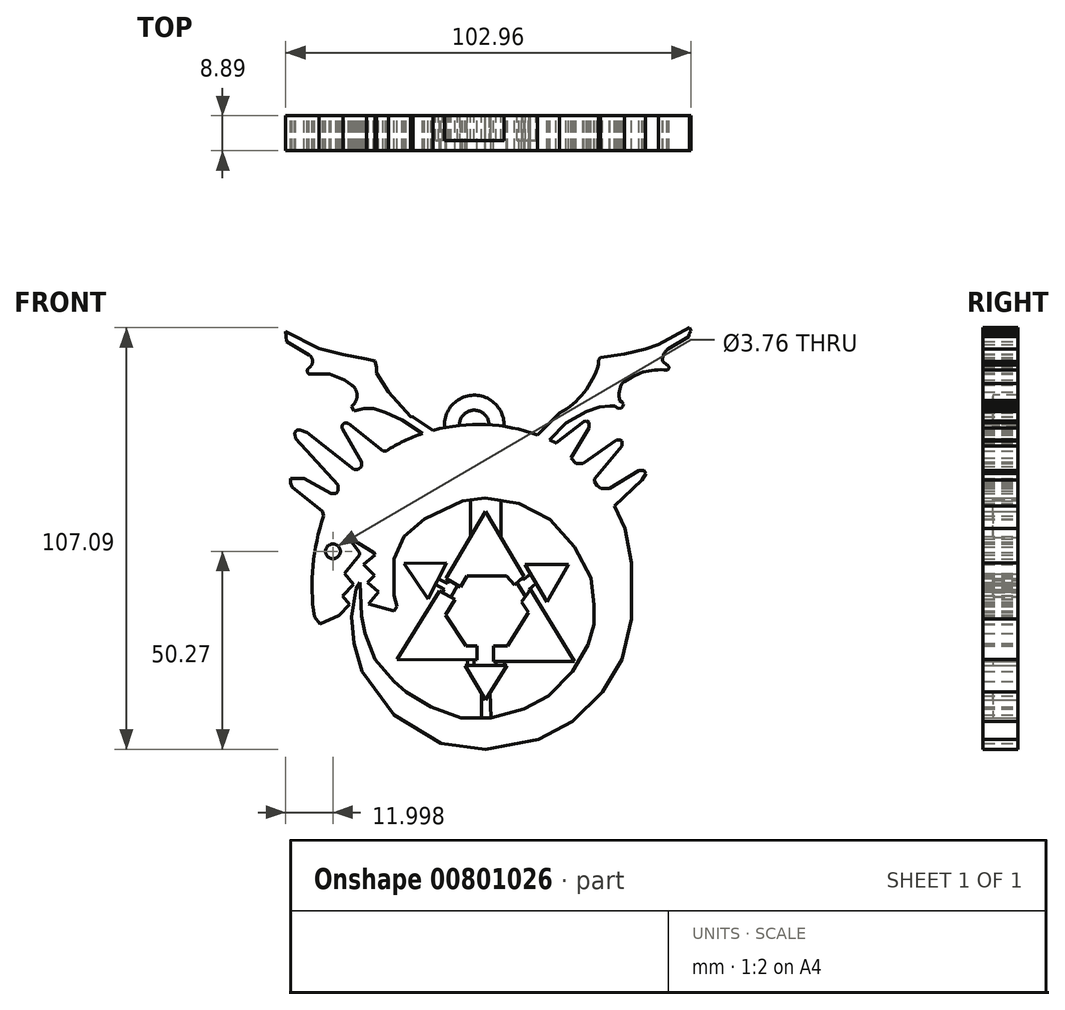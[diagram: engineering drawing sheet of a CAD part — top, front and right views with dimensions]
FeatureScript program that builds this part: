
annotation { "Feature Type Name" : "Feature", "Feature Type Description" : "" }
export const myFeature = defineFeature(function(context is Context, id is Id, definition is map)
    precondition{}
    {
        {
            var Q0;
            Q0=qCreatedBy(makeId("Front.planeOp"),FACE);
            var sketch = newSketch(context, id + "F0", { "sketchPlane" : qUnion([Q0])});
            skLineSegment(sketch, "E0", {"start": v(4.77, 15.18) * mm, "end": v(-5.28, -1.88) * mm});
            skLineSegment(sketch, "E1", {"start": v(-5.28, -1.88) * mm, "end": v(-1.66, -4) * mm});
            skLineSegment(sketch, "E2", {"start": v(-1.66, -4) * mm, "end": v(0, -1.18) * mm});
            skLineSegment(sketch, "E3", {"start": v(0, -1.18) * mm, "end": v(10.1, -1.18) * mm});
            skLineSegment(sketch, "E4", {"start": v(10.1, -1.18) * mm, "end": v(12.07, -3.5) * mm});
            skLineSegment(sketch, "E5", {"start": v(12.07, -3.5) * mm, "end": v(14.56, -1.36) * mm});
            skLineSegment(sketch, "E6", {"start": v(14.56, -1.36) * mm, "end": v(4.77, 15.18) * mm});
            skLineSegment(sketch, "E7", {"start": v(-15.93, 1.95) * mm, "end": v(-9.92, -7.03) * mm});
            skLineSegment(sketch, "E8", {"start": v(-9.92, -7.03) * mm, "end": v(-5.15, 2.13) * mm});
            skLineSegment(sketch, "E9", {"start": v(-5.15, 2.13) * mm, "end": v(-15.93, 1.95) * mm});
            skLineSegment(sketch, "E10", {"start": v(-6.9, -5.02) * mm, "end": v(-17.71, -22.44) * mm});
            skLineSegment(sketch, "E11", {"start": v(-17.71, -22.44) * mm, "end": v(2.58, -22.54) * mm});
            skLineSegment(sketch, "E12", {"start": v(-0.25, -18.9) * mm, "end": v(-5.46, -11.12) * mm});
            skLineSegment(sketch, "E13", {"start": v(-5.46, -11.12) * mm, "end": v(-2.97, -7.1) * mm});
            skLineSegment(sketch, "E14", {"start": v(-2.97, -7.1) * mm, "end": v(-6.9, -5.02) * mm});
            skLineSegment(sketch, "E15", {"start": v(13.84, -7.73) * mm, "end": v(15.64, -10.43) * mm});
            skLineSegment(sketch, "E16", {"start": v(15.64, -10.43) * mm, "end": v(10.38, -18.9) * mm});
            skLineSegment(sketch, "E17", {"start": v(10.38, -18.9) * mm, "end": v(6.72, -18.9) * mm});
            skLineSegment(sketch, "E18", {"start": v(6.72, -18.9) * mm, "end": v(6.72, -22.35) * mm});
            skLineSegment(sketch, "E19", {"start": v(6.72, -22.35) * mm, "end": v(6.72, -22.9) * mm});
            skLineSegment(sketch, "E20", {"start": v(6.72, -22.9) * mm, "end": v(27.35, -22.9) * mm});
            skLineSegment(sketch, "E21", {"start": v(27.35, -22.9) * mm, "end": v(16.18, -4.59) * mm});
            skLineSegment(sketch, "E22", {"start": v(16.18, -4.59) * mm, "end": v(13.84, -7.73) * mm});
            skLineSegment(sketch, "E23", {"start": v(14.74, 1.75) * mm, "end": v(25.78, 1.75) * mm});
            skPoint(sketch, "E23.startSnap0", {"position": v(14.74, -9.08) * mm});
            skLineSegment(sketch, "E24", {"start": v(25.78, 1.75) * mm, "end": v(20.37, -7.73) * mm});
            skLineSegment(sketch, "E25", {"start": v(20.37, -7.73) * mm, "end": v(14.74, 1.75) * mm});
            skLineSegment(sketch, "E26", {"start": v(4.77, -32.65) * mm, "end": v(10.23, -23.87) * mm});
            skLineSegment(sketch, "E27", {"start": v(10.23, -23.87) * mm, "end": v(-0.4, -23.87) * mm});
            skLineSegment(sketch, "E28", {"start": v(-0.4, -23.87) * mm, "end": v(4.77, -32.65) * mm});
            skCircle(sketch, "E29", {"center": v(-34.01, 5.06) * mm, "radius": 1.88 * mm});
            skLineSegment(sketch, "E30", {"start": v(-32.5, -11.2) * mm, "end": v(-29.8, -8.4) * mm});
            skLineSegment(sketch, "E31", {"start": v(-29.8, -8.4) * mm, "end": v(-31.63, -6.25) * mm});
            skLineSegment(sketch, "E32", {"start": v(-31.63, -6.25) * mm, "end": v(-28.79, -3.38) * mm});
            skLineSegment(sketch, "E33", {"start": v(-28.79, -3.38) * mm, "end": v(-31.12, -0.5) * mm});
            skLineSegment(sketch, "E34", {"start": v(-31.12, -0.5) * mm, "end": v(-27.2, 4.16) * mm});
            skLineSegment(sketch, "E35", {"start": v(-27.2, 4.16) * mm, "end": v(-27.2, 4.82) * mm});
            skLineSegment(sketch, "E36", {"start": v(-27.2, 4.82) * mm, "end": v(-29.33, 7.42) * mm});
            skLineSegment(sketch, "E37", {"start": v(-29.33, 7.42) * mm, "end": v(-29.33, 8.2) * mm});
            skLineSegment(sketch, "E38", {"start": v(-29.33, 8.2) * mm, "end": v(-23.64, 4.76) * mm});
            skLineSegment(sketch, "E39", {"start": v(-23.64, 4.76) * mm, "end": v(-23.31, 4.16) * mm});
            skLineSegment(sketch, "E40", {"start": v(-23.31, 4.16) * mm, "end": v(-26.21, 1.7) * mm});
            skLineSegment(sketch, "E41", {"start": v(-26.21, 1.7) * mm, "end": v(-23.4, -1.02) * mm});
            skLineSegment(sketch, "E42", {"start": v(-23.4, -1.02) * mm, "end": v(-25.2, -2.87) * mm});
            skLineSegment(sketch, "E43", {"start": v(-25.2, -2.87) * mm, "end": v(-22.4, -5.21) * mm});
            skLineSegment(sketch, "E44", {"start": v(-22.4, -5.21) * mm, "end": v(-25, -8.3) * mm});
            skLineSegment(sketch, "E45", {"start": v(-25, -8.3) * mm, "end": v(-18.52, -10.08) * mm});
            skLineSegment(sketch, "E46", {"start": v(-18.52, -10.08) * mm, "end": v(-17.79, -8.87) * mm});
            skLineSegment(sketch, "E47", {"start": v(-17.79, -8.87) * mm, "end": v(-18.52, -6.1) * mm});
            skLineSegment(sketch, "E48", {"start": v(-18.52, -6.1) * mm, "end": v(-18.52, 3.16) * mm});
            skLineSegment(sketch, "E49", {"start": v(-18.52, 3.16) * mm, "end": v(-15.99, 8.85) * mm});
            skLineSegment(sketch, "E50", {"start": v(-15.99, 8.85) * mm, "end": v(-10.8, 13.27) * mm});
            skLineSegment(sketch, "E51", {"start": v(-10.8, 13.27) * mm, "end": v(-1.11, 17.82) * mm});
            skLineSegment(sketch, "E52", {"start": v(-1.11, 17.82) * mm, "end": v(4.58, 18.6) * mm});
            skLineSegment(sketch, "E53", {"start": v(4.58, 18.6) * mm, "end": v(13.19, 17.25) * mm});
            skLineSegment(sketch, "E54", {"start": v(13.19, 17.25) * mm, "end": v(21.16, 13.12) * mm});
            skLineSegment(sketch, "E55", {"start": v(21.16, 13.12) * mm, "end": v(27.35, 6.15) * mm});
            skLineSegment(sketch, "E56", {"start": v(27.35, 6.15) * mm, "end": v(31.48, -1.68) * mm});
            skLineSegment(sketch, "E57", {"start": v(31.48, -1.68) * mm, "end": v(32.26, -8.5) * mm});
            skLineSegment(sketch, "E58", {"start": v(32.26, -8.5) * mm, "end": v(32.26, -13.52) * mm});
            skLineSegment(sketch, "E59", {"start": v(32.26, -13.52) * mm, "end": v(30.8, -18.77) * mm});
            skLineSegment(sketch, "E60", {"start": v(30.8, -18.77) * mm, "end": v(26.81, -25.37) * mm});
            skLineSegment(sketch, "E61", {"start": v(26.81, -25.37) * mm, "end": v(20.73, -31.63) * mm});
            skLineSegment(sketch, "E62", {"start": v(20.73, -31.63) * mm, "end": v(14.46, -34.93) * mm});
            skLineSegment(sketch, "E63", {"start": v(14.46, -34.93) * mm, "end": v(6.1, -37.3) * mm});
            skLineSegment(sketch, "E64", {"start": v(6.1, -37.3) * mm, "end": v(-1.53, -37.3) * mm});
            skLineSegment(sketch, "E65", {"start": v(-1.53, -37.3) * mm, "end": v(-9.14, -34.42) * mm});
            skLineSegment(sketch, "E66", {"start": v(-9.14, -34.42) * mm, "end": v(-15.41, -30.63) * mm});
            skLineSegment(sketch, "E67", {"start": v(-15.41, -30.63) * mm, "end": v(-18.52, -27.99) * mm});
            skLineSegment(sketch, "E68", {"start": v(-18.52, -27.99) * mm, "end": v(-23.31, -22.44) * mm});
            skLineSegment(sketch, "E69", {"start": v(-23.31, -22.44) * mm, "end": v(-25.82, -15.8) * mm});
            skLineSegment(sketch, "E70", {"start": v(-25.82, -15.8) * mm, "end": v(-26.75, -11.32) * mm});
            skLineSegment(sketch, "E71", {"start": v(-26.75, -11.32) * mm, "end": v(-27.17, -2.84) * mm});
            skLineSegment(sketch, "E72", {"start": v(-27.17, -2.84) * mm, "end": v(-28.18, -4.51) * mm});
            skLineSegment(sketch, "E73", {"start": v(-28.18, -4.51) * mm, "end": v(-29.33, -11.55) * mm});
            skLineSegment(sketch, "E74", {"start": v(-29.33, -11.55) * mm, "end": v(-28.6, -18.28) * mm});
            skLineSegment(sketch, "E75", {"start": v(-28.6, -18.28) * mm, "end": v(-26.58, -25.37) * mm});
            skLineSegment(sketch, "E76", {"start": v(-26.58, -25.37) * mm, "end": v(-18.52, -36.53) * mm});
            skLineSegment(sketch, "E77", {"start": v(-18.52, -36.53) * mm, "end": v(-6.54, -43.78) * mm});
            skLineSegment(sketch, "E78", {"start": v(-6.54, -43.78) * mm, "end": v(4.73, -45.2) * mm});
            skLineSegment(sketch, "E79", {"start": v(4.73, -45.2) * mm, "end": v(18.25, -42.65) * mm});
            skLineSegment(sketch, "E80", {"start": v(18.25, -42.65) * mm, "end": v(26.81, -38.13) * mm});
            skLineSegment(sketch, "E81", {"start": v(26.81, -38.13) * mm, "end": v(34.43, -30.63) * mm});
            skLineSegment(sketch, "E82", {"start": v(34.43, -30.63) * mm, "end": v(39.38, -22.44) * mm});
            skLineSegment(sketch, "E83", {"start": v(39.38, -22.44) * mm, "end": v(41.88, -12.05) * mm});
            skLineSegment(sketch, "E84", {"start": v(41.88, -12.05) * mm, "end": v(41.88, -4.5) * mm});
            skLineSegment(sketch, "E85", {"start": v(41.88, -4.5) * mm, "end": v(41.88, 2.13) * mm});
            skLineSegment(sketch, "E86", {"start": v(41.88, 2.13) * mm, "end": v(40.17, 10.94) * mm});
            skLineSegment(sketch, "E87", {"start": v(40.17, 10.94) * mm, "end": v(37.53, 16.63) * mm});
            skLineSegment(sketch, "E88", {"start": v(37.53, 16.63) * mm, "end": v(44.45, 23.16) * mm});
            skLineSegment(sketch, "E89", {"start": v(44.45, 23.16) * mm, "end": v(45.46, 24.84) * mm});
            skLineSegment(sketch, "E90", {"start": v(45.46, 24.84) * mm, "end": v(44.99, 25.62) * mm});
            skLineSegment(sketch, "E91", {"start": v(44.99, 25.62) * mm, "end": v(43.77, 25.62) * mm});
            skLineSegment(sketch, "E92", {"start": v(43.77, 25.62) * mm, "end": v(36.18, 20.99) * mm});
            skLineSegment(sketch, "E93", {"start": v(36.18, 20.99) * mm, "end": v(34.08, 20.99) * mm});
            skLineSegment(sketch, "E94", {"start": v(34.08, 20.99) * mm, "end": v(33.06, 21.75) * mm});
            skLineSegment(sketch, "E95", {"start": v(33.06, 21.75) * mm, "end": v(32.41, 22.8) * mm});
            skLineSegment(sketch, "E96", {"start": v(32.41, 22.8) * mm, "end": v(32.41, 23.5) * mm});
            skLineSegment(sketch, "E97", {"start": v(32.41, 23.5) * mm, "end": v(39.38, 31.8) * mm});
            skLineSegment(sketch, "E98", {"start": v(39.38, 31.8) * mm, "end": v(39.38, 33.07) * mm});
            skLineSegment(sketch, "E99", {"start": v(39.38, 33.07) * mm, "end": v(38.93, 33.34) * mm});
            skLineSegment(sketch, "E100", {"start": v(38.93, 33.34) * mm, "end": v(38, 33.34) * mm});
            skLineSegment(sketch, "E101", {"start": v(38, 33.34) * mm, "end": v(29.49, 27.43) * mm});
            skLineSegment(sketch, "E102", {"start": v(29.49, 27.43) * mm, "end": v(27.73, 27.43) * mm});
            skLineSegment(sketch, "E103", {"start": v(27.73, 27.43) * mm, "end": v(26.47, 28.76) * mm});
            skLineSegment(sketch, "E104", {"start": v(26.47, 28.76) * mm, "end": v(31.1, 36.38) * mm});
            skLineSegment(sketch, "E105", {"start": v(31.1, 36.38) * mm, "end": v(31.1, 37.8) * mm});
            skLineSegment(sketch, "E106", {"start": v(31.1, 37.8) * mm, "end": v(30.4, 38.22) * mm});
            skLineSegment(sketch, "E107", {"start": v(30.4, 38.22) * mm, "end": v(29.76, 38.09) * mm});
            skLineSegment(sketch, "E108", {"start": v(29.76, 38.09) * mm, "end": v(22.7, 32.6) * mm});
            skArc(sketch, "E109", {"start": v(22.7, 32.6) * mm, "mid": v(0.86, 37.28) * mm, "end": v(-20.46, 30.63) * mm});
            skArc(sketch, "E110", {"start": v(-30.1, 37.53) * mm, "mid": v(-31.37, 37.44) * mm, "end": v(-31.62, 36.2) * mm});
            skLineSegment(sketch, "E111", {"start": v(-20.46, 30.63) * mm, "end": v(-21.26, 30.63) * mm});
            skLineSegment(sketch, "E112", {"start": v(-21.26, 30.63) * mm, "end": v(-30.1, 37.53) * mm});
            skLineSegment(sketch, "E113", {"start": v(-31.62, 36.2) * mm, "end": v(-26.72, 27.83) * mm});
            skLineSegment(sketch, "E114", {"start": v(-26.72, 27.83) * mm, "end": v(-26.72, 26.6) * mm});
            skLineSegment(sketch, "E115", {"start": v(-26.72, 26.6) * mm, "end": v(-27.67, 25.86) * mm});
            skLineSegment(sketch, "E116", {"start": v(-27.67, 25.86) * mm, "end": v(-28.69, 25.86) * mm});
            skLineSegment(sketch, "E117", {"start": v(-28.69, 25.86) * mm, "end": v(-40.57, 35.26) * mm});
            skLineSegment(sketch, "E118", {"start": v(-40.57, 35.26) * mm, "end": v(-42.4, 35.88) * mm});
            skArc(sketch, "E119", {"start": v(-42.4, 35.88) * mm, "mid": v(-43.4, 35.67) * mm, "end": v(-43.7, 34.7) * mm});
            skLineSegment(sketch, "E120", {"start": v(-43.7, 34.7) * mm, "end": v(-43.48, 33.8) * mm});
            skLineSegment(sketch, "E121", {"start": v(-43.48, 33.8) * mm, "end": v(-32.73, 21.9) * mm});
            skLineSegment(sketch, "E122", {"start": v(-32.73, 21.9) * mm, "end": v(-32.73, 20.45) * mm});
            skLineSegment(sketch, "E123", {"start": v(-32.73, 20.45) * mm, "end": v(-33.26, 19.82) * mm});
            skLineSegment(sketch, "E124", {"start": v(-33.26, 19.82) * mm, "end": v(-34.5, 19.82) * mm});
            skLineSegment(sketch, "E125", {"start": v(-34.5, 19.82) * mm, "end": v(-41.36, 23.6) * mm});
            skLineSegment(sketch, "E126", {"start": v(-41.36, 23.6) * mm, "end": v(-44.73, 23.6) * mm});
            skLineSegment(sketch, "E127", {"start": v(-44.73, 23.6) * mm, "end": v(-44.73, 22.4) * mm});
            skLineSegment(sketch, "E128", {"start": v(-44.73, 22.4) * mm, "end": v(-44.37, 21.49) * mm});
            skLineSegment(sketch, "E129", {"start": v(-44.37, 21.49) * mm, "end": v(-36.61, 15.2) * mm});
            skLineSegment(sketch, "E130", {"start": v(-36.61, 15.2) * mm, "end": v(-36.34, 14.07) * mm});
            skArc(sketch, "E131", {"start": v(-36.34, 14.07) * mm, "mid": v(-39.1, 1.4) * mm, "end": v(-38.75, -11.56) * mm});
            skLineSegment(sketch, "E132", {"start": v(-38.75, -11.56) * mm, "end": v(-37.29, -13.35) * mm});
            skLineSegment(sketch, "E133", {"start": v(-37.29, -13.35) * mm, "end": v(-32.5, -11.2) * mm});
            skArc(sketch, "E134", {"start": v(-29.27, 41.92) * mm, "mid": v(-27.89, 44.65) * mm, "end": v(-29.27, 47.38) * mm});
            skLineSegment(sketch, "E135", {"start": v(-29.27, 41.92) * mm, "end": v(-28.61, 40.78) * mm});
            skLineSegment(sketch, "E136", {"start": v(-28.61, 40.78) * mm, "end": v(-26.1, 41.38) * mm});
            skLineSegment(sketch, "E137", {"start": v(-26.1, 41.38) * mm, "end": v(-23.7, 41.38) * mm});
            skLineSegment(sketch, "E138", {"start": v(-23.7, 41.38) * mm, "end": v(-20.64, 40.36) * mm});
            skLineSegment(sketch, "E139", {"start": v(-20.64, 40.36) * mm, "end": v(-16.5, 38.5) * mm});
            skLineSegment(sketch, "E140", {"start": v(-16.5, 38.5) * mm, "end": v(-14.88, 37.43) * mm});
            skArc(sketch, "E141", {"start": v(-14.88, 37.43) * mm, "mid": v(-13.38, 37.73) * mm, "end": v(-13.68, 39.22) * mm});
            skLineSegment(sketch, "E142", {"start": v(-13.68, 39.22) * mm, "end": v(-14.28, 39.28) * mm});
            skLineSegment(sketch, "E143", {"start": v(-14.28, 39.28) * mm, "end": v(-19.92, 45.52) * mm});
            skLineSegment(sketch, "E144", {"start": v(-19.92, 45.52) * mm, "end": v(-22.9, 50.42) * mm});
            skLineSegment(sketch, "E145", {"start": v(-22.9, 50.42) * mm, "end": v(-22.9, 51.72) * mm});
            skLineSegment(sketch, "E146", {"start": v(-22.9, 51.72) * mm, "end": v(-23.36, 53.43) * mm});
            skLineSegment(sketch, "E147", {"start": v(-23.36, 53.43) * mm, "end": v(-25.48, 53.9) * mm});
            skLineSegment(sketch, "E148", {"start": v(-25.48, 53.9) * mm, "end": v(-31.48, 55.1) * mm});
            skLineSegment(sketch, "E149", {"start": v(-31.48, 55.1) * mm, "end": v(-37.56, 56.6) * mm});
            skLineSegment(sketch, "E150", {"start": v(-37.56, 56.6) * mm, "end": v(-46.01, 60.86) * mm});
            skLineSegment(sketch, "E151", {"start": v(-46.01, 60.86) * mm, "end": v(-45.83, 58.38) * mm});
            skLineSegment(sketch, "E152", {"start": v(-45.83, 58.38) * mm, "end": v(-40.08, 54.95) * mm});
            skArc(sketch, "E153", {"start": v(-40.08, 51.74) * mm, "mid": v(-39.17, 53.35) * mm, "end": v(-40.08, 54.95) * mm});
            skArc(sketch, "E154", {"start": v(-40.08, 51.74) * mm, "mid": v(-40.54, 50.92) * mm, "end": v(-40.08, 50.1) * mm});
            skLineSegment(sketch, "E155", {"start": v(-40.08, 50.1) * mm, "end": v(-34.82, 50.1) * mm});
            skLineSegment(sketch, "E156", {"start": v(-34.82, 50.1) * mm, "end": v(-31.12, 48.66) * mm});
            skLineSegment(sketch, "E157", {"start": v(-31.12, 48.66) * mm, "end": v(-29.27, 47.38) * mm});
            skArc(sketch, "E158", {"start": v(39.45, 47.68) * mm, "mid": v(38.74, 45.62) * mm, "end": v(38.82, 43.45) * mm});
            skArc(sketch, "E159", {"start": v(50.85, 51.1) * mm, "mid": v(44.8, 50.57) * mm, "end": v(39.45, 47.68) * mm});
            skArc(sketch, "E160", {"start": v(50.85, 51.1) * mm, "mid": v(51.32, 51.76) * mm, "end": v(50.85, 52.42) * mm});
            skLineSegment(sketch, "E161", {"start": v(50.85, 52.42) * mm, "end": v(49.8, 53.26) * mm});
            skArc(sketch, "E162", {"start": v(51.11, 56.48) * mm, "mid": v(49.97, 55.07) * mm, "end": v(49.8, 53.26) * mm});
            skLineSegment(sketch, "E163", {"start": v(51.11, 56.48) * mm, "end": v(56.4, 59.66) * mm});
            skLineSegment(sketch, "E164", {"start": v(56.4, 59.66) * mm, "end": v(56.4, 60.26) * mm});
            skLineSegment(sketch, "E165", {"start": v(56.4, 60.26) * mm, "end": v(56.95, 61.1) * mm});
            skLineSegment(sketch, "E166", {"start": v(56.95, 61.1) * mm, "end": v(56.6, 61.88) * mm});
            skLineSegment(sketch, "E167", {"start": v(56.6, 61.88) * mm, "end": v(48.64, 57.64) * mm});
            skLineSegment(sketch, "E168", {"start": v(48.64, 57.64) * mm, "end": v(45.37, 56.48) * mm});
            skLineSegment(sketch, "E169", {"start": v(45.37, 56.48) * mm, "end": v(40.08, 55.2) * mm});
            skLineSegment(sketch, "E170", {"start": v(40.08, 55.2) * mm, "end": v(35.01, 54.46) * mm});
            skLineSegment(sketch, "E171", {"start": v(35.01, 54.46) * mm, "end": v(34, 54.31) * mm});
            skLineSegment(sketch, "E172", {"start": v(34, 54.31) * mm, "end": v(33.45, 53.66) * mm});
            skLineSegment(sketch, "E173", {"start": v(33.45, 53.66) * mm, "end": v(33.45, 52.6) * mm});
            skArc(sketch, "E174", {"start": v(23.59, 40.22) * mm, "mid": v(29.76, 45.42) * mm, "end": v(33.45, 52.6) * mm});
            skLineSegment(sketch, "E175", {"start": v(23.59, 40.22) * mm, "end": v(23, 39.25) * mm});
            skLineSegment(sketch, "E176", {"start": v(23, 39.25) * mm, "end": v(23.33, 37.92) * mm});
            skLineSegment(sketch, "E177", {"start": v(23.33, 37.92) * mm, "end": v(23.59, 37.66) * mm});
            skLineSegment(sketch, "E178", {"start": v(23.59, 37.66) * mm, "end": v(25.2, 37.65) * mm});
            skLineSegment(sketch, "E179", {"start": v(25.2, 37.65) * mm, "end": v(30.4, 40.62) * mm});
            skLineSegment(sketch, "E180", {"start": v(30.4, 40.62) * mm, "end": v(33.68, 41.71) * mm});
            skLineSegment(sketch, "E181", {"start": v(33.68, 41.71) * mm, "end": v(36.34, 42) * mm});
            skLineSegment(sketch, "E182", {"start": v(36.34, 42) * mm, "end": v(37.67, 42) * mm});
            skLineSegment(sketch, "E183", {"start": v(37.67, 42) * mm, "end": v(38.45, 41.4) * mm});
            skLineSegment(sketch, "E184", {"start": v(38.45, 41.4) * mm, "end": v(39.25, 41.53) * mm});
            skLineSegment(sketch, "E185", {"start": v(39.25, 41.53) * mm, "end": v(39.68, 42) * mm});
            skLineSegment(sketch, "E186", {"start": v(39.68, 42) * mm, "end": v(39.85, 42.57) * mm});
            skLineSegment(sketch, "E187", {"start": v(39.85, 42.57) * mm, "end": v(39.47, 43.02) * mm});
            skLineSegment(sketch, "E188", {"start": v(39.47, 43.02) * mm, "end": v(38.82, 43.45) * mm});
            skLineSegment(sketch, "E189", {"start": v(-4.51, -2.33) * mm, "end": v(-4.94, -3.13) * mm});
            skLineSegment(sketch, "E190", {"start": v(-2.33, -3.61) * mm, "end": v(-4.05, -6.53) * mm});
            skPoint(sketch, "E191.endSnap0", {"position": v(15.01, -6.16) * mm});
            skLineSegment(sketch, "E192", {"start": v(15.96, -4.9) * mm, "end": v(15.81, -4.66) * mm});
            skLineSegment(sketch, "E193", {"start": v(12.73, -2.93) * mm, "end": v(14.84, -6.39) * mm});
            skLineSegment(sketch, "E194", {"start": v(0.18, -22.53) * mm, "end": v(0.18, -23.87) * mm});
            skLineSegment(sketch, "E195", {"start": v(1.8, -22.54) * mm, "end": v(1.8, -23.87) * mm});
            skLineSegment(sketch, "E196", {"start": v(7.37, -22.9) * mm, "end": v(7.37, -23.87) * mm});
            skLineSegment(sketch, "E197", {"start": v(9.53, -22.9) * mm, "end": v(9.53, -23.87) * mm});
            skLineSegment(sketch, "E198", {"start": v(-14.88, 37.43) * mm, "end": v(-11.25, 35) * mm});
            skLineSegment(sketch, "E199", {"start": v(-13.68, 39.22) * mm, "end": v(-8.57, 35.81) * mm});
            skLineSegment(sketch, "E200", {"start": v(23.59, 40.22) * mm, "end": v(18, 34.63) * mm});
            skLineSegment(sketch, "E201", {"start": v(25.2, 37.65) * mm, "end": v(20.97, 33.42) * mm});
            skLineSegment(sketch, "E202", {"start": v(-5.71, -4.6) * mm, "end": v(-8.02, -3.39) * mm});
            skLineSegment(sketch, "E203", {"start": v(-4.94, -3.13) * mm, "end": v(-7.25, -1.9) * mm});
            skLineSegment(sketch, "E204", {"start": v(14.33, -2.22) * mm, "end": v(16.16, -0.64) * mm});
            skPoint(sketch, "E205.startSnap0", {"position": v(13.79, -4.66) * mm});
            skLineSegment(sketch, "E206", {"start": v(0.9, 8.6) * mm, "end": v(0.9, 18.1) * mm});
            skLineSegment(sketch, "E207", {"start": v(8.66, 8.6) * mm, "end": v(8.66, 17.96) * mm});
            skLineSegment(sketch, "E208", {"start": v(3.69, -30.81) * mm, "end": v(3.69, -37.3) * mm});
            skLineSegment(sketch, "E209", {"start": v(5.92, -30.81) * mm, "end": v(6.1, -37.3) * mm});
            skLineSegment(sketch, "E210", {"start": v(15.81, -4.66) * mm, "end": v(17.62, -3.1) * mm});
            skLineSegment(sketch, "E211", {"start": v(2.58, -22.54) * mm, "end": v(2.58, -18.9) * mm});
            skLineSegment(sketch, "E212", {"start": v(2.58, -18.9) * mm, "end": v(-0.25, -18.9) * mm});
            skLineSegment(sketch, "E213.trimOffspring", {"start": v(-5.71, -4.6) * mm, "end": v(-6.15, -5.42) * mm});
            skLineSegment(sketch, "E214.trimOffspring", {"start": v(14.33, -2.22) * mm, "end": v(14.06, -1.79) * mm});
            skSolve(sketch);
        }
        {
            var Q0;
            Q0=makeQuery(id+"F0.imprint","IMPRINT",FACE,{"disambiguationData":[TD([[makeQuery(id+"F0.imprint","IMPRINT",EDGE,{"derivedFrom":sQuery(id+"F0.wireOp",EDGE,"E29")}),-1.0]])]});
            var Q1;
            Q1=makeQuery(id+"F0.imprint","IMPRINT",FACE,{"disambiguationData":[TD([[makeQuery(id+"F0.imprint","IMPRINT",EDGE,{"derivedFrom":sQuery(id+"F0.wireOp",EDGE,"E158")}),-1.0]])]});
            var Q2;
            Q2=makeQuery(id+"F0.imprint","IMPRINT",FACE,{"disambiguationData":[TD([[makeQuery(id+"F0.imprint","IMPRINT",EDGE,{"derivedFrom":sQuery(id+"F0.wireOp",EDGE,"E175")}),-1.0]])]});
            var Q3;
            Q3=makeQuery(id+"F0.imprint","IMPRINT",FACE,{"disambiguationData":[TD([[makeQuery(id+"F0.imprint","IMPRINT",EDGE,{"derivedFrom":sQuery(id+"F0.wireOp",EDGE,"E134")}),-1.0]])]});
            var Q4;
            Q4=makeQuery(id+"F0.imprint","IMPRINT",FACE,{"disambiguationData":[TD([[makeQuery(id+"F0.imprint","IMPRINT",EDGE,{"derivedFrom":sQuery(id+"F0.wireOp",EDGE,"E141")}),-1.0]])]});
            var Q5;
            {var subQ4=sQuery(id+"F0.wireOp",EDGE,"E2");Q5=makeQuery(id+"F0.imprint","IMPRINT",FACE,{"disambiguationData":[TD([[makeQuery(id+"F0.imprint","IMPRINT",EDGE,{"derivedFrom":subQ4}),1.0]])]});}
            var Q6;
            {var subQ4=sQuery(id+"F0.wireOp",EDGE,"E23");Q6=makeQuery(id+"F0.imprint","IMPRINT",FACE,{"disambiguationData":[TD([[makeQuery(id+"F0.imprint","IMPRINT",EDGE,{"derivedFrom":subQ4}),-1.0]])]});}
            var Q7;
            {var subQ7=sQuery(id+"F0.wireOp",EDGE,"E15");Q7=makeQuery(id+"F0.imprint","IMPRINT",FACE,{"disambiguationData":[TD([[makeQuery(id+"F0.imprint","IMPRINT",EDGE,{"derivedFrom":subQ7}),1.0]])]});}
            var Q8;
            {var subQ4=sQuery(id+"F0.wireOp",EDGE,"E10");Q8=makeQuery(id+"F0.imprint","IMPRINT",FACE,{"disambiguationData":[TD([[makeQuery(id+"F0.imprint","IMPRINT",EDGE,{"derivedFrom":subQ4}),1.0]])]});}
            var Q9;
            {var subQ3=sQuery(id+"F0.wireOp",EDGE,"E26");var subQ6=sQuery(id+"F0.wireOp",EDGE,"E28");var subQ7=makeQuery(id+"F0.imprint","INTERSECT",VERTEX,{"derivedFrom":[subQ3,subQ6]});Q9=makeQuery(id+"F0.imprint","IMPRINT",FACE,{"disambiguationData":[TD([[makeQuery(id+"F0.imprint","IMPRINT",EDGE,{"disambiguationData":[TD([[subQ7,-1.0]])],"derivedFrom":subQ3}),1.0]])]});}
            var Q10;
            {var subQ4=sQuery(id+"F0.wireOp",EDGE,"E7");Q10=makeQuery(id+"F0.imprint","IMPRINT",FACE,{"disambiguationData":[TD([[makeQuery(id+"F0.imprint","IMPRINT",EDGE,{"derivedFrom":subQ4}),1.0]])]});}
            extrude(context, id + "F1", {"entities" : qUnion([Q0, Q1, Q2, Q3, Q4, Q5, Q6, Q7, Q8, Q9, Q10]), "depth" : 8.9 * mm, "offsetDistance" : 25.4 * mm});
        }
        {
            var Q0;
            {var subQ7=sQuery(id+"F0.wireOp",EDGE,"E206");Q0=makeQuery(id+"F0.imprint","IMPRINT",FACE,{"disambiguationData":[TD([[makeQuery(id+"F0.imprint","IMPRINT",EDGE,{"derivedFrom":subQ7}),-1.0]])]});}
            var Q1;
            {var subQ5=sQuery(id+"F0.wireOp",EDGE,"E190");Q1=makeQuery(id+"F0.imprint","IMPRINT",FACE,{"disambiguationData":[TD([[makeQuery(id+"F0.imprint","IMPRINT",EDGE,{"derivedFrom":subQ5}),-1.0]])]});}
            var Q2;
            {var subQ0=sQuery(id+"F0.wireOp",EDGE,"E202");Q2=makeQuery(id+"F0.imprint","IMPRINT",FACE,{"disambiguationData":[TD([[makeQuery(id+"F0.imprint","IMPRINT",EDGE,{"derivedFrom":subQ0}),-1.0]])]});}
            var Q3;
            {var subQ0=sQuery(id+"F0.wireOp",EDGE,"E204");Q3=makeQuery(id+"F0.imprint","IMPRINT",FACE,{"disambiguationData":[TD([[makeQuery(id+"F0.imprint","IMPRINT",EDGE,{"derivedFrom":subQ0}),-1.0]])]});}
            var Q4;
            {var subQ5=sQuery(id+"F0.wireOp",EDGE,"E193");Q4=makeQuery(id+"F0.imprint","IMPRINT",FACE,{"disambiguationData":[TD([[makeQuery(id+"F0.imprint","IMPRINT",EDGE,{"derivedFrom":subQ5}),1.0]])]});}
            var Q5;
            {var subQ0=sQuery(id+"F0.wireOp",EDGE,"E194");Q5=makeQuery(id+"F0.imprint","IMPRINT",FACE,{"disambiguationData":[TD([[makeQuery(id+"F0.imprint","IMPRINT",EDGE,{"derivedFrom":subQ0}),1.0]])]});}
            var Q6;
            {var subQ0=sQuery(id+"F0.wireOp",EDGE,"E196");Q6=makeQuery(id+"F0.imprint","IMPRINT",FACE,{"disambiguationData":[TD([[makeQuery(id+"F0.imprint","IMPRINT",EDGE,{"derivedFrom":subQ0}),1.0]])]});}
            var Q7;
            {var subQ0=sQuery(id+"F0.wireOp",EDGE,"E208");Q7=makeQuery(id+"F0.imprint","IMPRINT",FACE,{"disambiguationData":[TD([[makeQuery(id+"F0.imprint","IMPRINT",EDGE,{"derivedFrom":subQ0}),1.0]])]});}
            extrude(context, id + "F2", {"entities" : qUnion([Q0, Q1, Q2, Q3, Q4, Q5, Q6, Q7]), "depth" : 6.35 * mm, "offsetDistance" : 25.4 * mm});
        }
        {
            var Q0;
            Q0=makeQuery(id+"F1.opExtrude","CAP_FACE",FACE,{"disambiguationData":[OSD([sQuery(id+"F0.wireOp",EDGE,"E29"),sQuery(id+"F0.wireOp",EDGE,"E30"),sQuery(id+"F0.wireOp",EDGE,"E31"),sQuery(id+"F0.wireOp",EDGE,"E32"),sQuery(id+"F0.wireOp",EDGE,"E33"),sQuery(id+"F0.wireOp",EDGE,"E34"),sQuery(id+"F0.wireOp",EDGE,"E35"),sQuery(id+"F0.wireOp",EDGE,"E36"),sQuery(id+"F0.wireOp",EDGE,"E37"),sQuery(id+"F0.wireOp",EDGE,"E38"),sQuery(id+"F0.wireOp",EDGE,"E39"),sQuery(id+"F0.wireOp",EDGE,"E40"),sQuery(id+"F0.wireOp",EDGE,"E41"),sQuery(id+"F0.wireOp",EDGE,"E42"),sQuery(id+"F0.wireOp",EDGE,"E43"),sQuery(id+"F0.wireOp",EDGE,"E44"),sQuery(id+"F0.wireOp",EDGE,"E45"),sQuery(id+"F0.wireOp",EDGE,"E46"),sQuery(id+"F0.wireOp",EDGE,"E47"),sQuery(id+"F0.wireOp",EDGE,"E48"),sQuery(id+"F0.wireOp",EDGE,"E49"),sQuery(id+"F0.wireOp",EDGE,"E50"),sQuery(id+"F0.wireOp",EDGE,"E51"),sQuery(id+"F0.wireOp",EDGE,"E52"),sQuery(id+"F0.wireOp",EDGE,"E53"),sQuery(id+"F0.wireOp",EDGE,"E54"),sQuery(id+"F0.wireOp",EDGE,"E55"),sQuery(id+"F0.wireOp",EDGE,"E56"),sQuery(id+"F0.wireOp",EDGE,"E57"),sQuery(id+"F0.wireOp",EDGE,"E58"),sQuery(id+"F0.wireOp",EDGE,"E59"),sQuery(id+"F0.wireOp",EDGE,"E60"),sQuery(id+"F0.wireOp",EDGE,"E61"),sQuery(id+"F0.wireOp",EDGE,"E62"),sQuery(id+"F0.wireOp",EDGE,"E63"),sQuery(id+"F0.wireOp",EDGE,"E64"),sQuery(id+"F0.wireOp",EDGE,"E65"),sQuery(id+"F0.wireOp",EDGE,"E66"),sQuery(id+"F0.wireOp",EDGE,"E67"),sQuery(id+"F0.wireOp",EDGE,"E68"),sQuery(id+"F0.wireOp",EDGE,"E69"),sQuery(id+"F0.wireOp",EDGE,"E70"),sQuery(id+"F0.wireOp",EDGE,"E71"),sQuery(id+"F0.wireOp",EDGE,"E72"),sQuery(id+"F0.wireOp",EDGE,"E73"),sQuery(id+"F0.wireOp",EDGE,"E74"),sQuery(id+"F0.wireOp",EDGE,"E75"),sQuery(id+"F0.wireOp",EDGE,"E76"),sQuery(id+"F0.wireOp",EDGE,"E77"),sQuery(id+"F0.wireOp",EDGE,"E78"),sQuery(id+"F0.wireOp",EDGE,"E79"),sQuery(id+"F0.wireOp",EDGE,"E80"),sQuery(id+"F0.wireOp",EDGE,"E81"),sQuery(id+"F0.wireOp",EDGE,"E82"),sQuery(id+"F0.wireOp",EDGE,"E83"),sQuery(id+"F0.wireOp",EDGE,"E84"),sQuery(id+"F0.wireOp",EDGE,"E85"),sQuery(id+"F0.wireOp",EDGE,"E86"),sQuery(id+"F0.wireOp",EDGE,"E87"),sQuery(id+"F0.wireOp",EDGE,"E88"),sQuery(id+"F0.wireOp",EDGE,"E89"),sQuery(id+"F0.wireOp",EDGE,"E90"),sQuery(id+"F0.wireOp",EDGE,"E91"),sQuery(id+"F0.wireOp",EDGE,"E92"),sQuery(id+"F0.wireOp",EDGE,"E93"),sQuery(id+"F0.wireOp",EDGE,"E94"),sQuery(id+"F0.wireOp",EDGE,"E95"),sQuery(id+"F0.wireOp",EDGE,"E96"),sQuery(id+"F0.wireOp",EDGE,"E97"),sQuery(id+"F0.wireOp",EDGE,"E98"),sQuery(id+"F0.wireOp",EDGE,"E99"),sQuery(id+"F0.wireOp",EDGE,"E100"),sQuery(id+"F0.wireOp",EDGE,"E101"),sQuery(id+"F0.wireOp",EDGE,"E102"),sQuery(id+"F0.wireOp",EDGE,"E103"),sQuery(id+"F0.wireOp",EDGE,"E104"),sQuery(id+"F0.wireOp",EDGE,"E105"),sQuery(id+"F0.wireOp",EDGE,"E106"),sQuery(id+"F0.wireOp",EDGE,"E107"),sQuery(id+"F0.wireOp",EDGE,"E108"),sQuery(id+"F0.wireOp",EDGE,"E109"),sQuery(id+"F0.wireOp",EDGE,"E110"),sQuery(id+"F0.wireOp",EDGE,"E111"),sQuery(id+"F0.wireOp",EDGE,"E112"),sQuery(id+"F0.wireOp",EDGE,"E113"),sQuery(id+"F0.wireOp",EDGE,"E114"),sQuery(id+"F0.wireOp",EDGE,"E115"),sQuery(id+"F0.wireOp",EDGE,"E116"),sQuery(id+"F0.wireOp",EDGE,"E117"),sQuery(id+"F0.wireOp",EDGE,"E118"),sQuery(id+"F0.wireOp",EDGE,"E119"),sQuery(id+"F0.wireOp",EDGE,"E120"),sQuery(id+"F0.wireOp",EDGE,"E121"),sQuery(id+"F0.wireOp",EDGE,"E122"),sQuery(id+"F0.wireOp",EDGE,"E123"),sQuery(id+"F0.wireOp",EDGE,"E124"),sQuery(id+"F0.wireOp",EDGE,"E125"),sQuery(id+"F0.wireOp",EDGE,"E126"),sQuery(id+"F0.wireOp",EDGE,"E127"),sQuery(id+"F0.wireOp",EDGE,"E128"),sQuery(id+"F0.wireOp",EDGE,"E129"),sQuery(id+"F0.wireOp",EDGE,"E130"),sQuery(id+"F0.wireOp",EDGE,"E131"),sQuery(id+"F0.wireOp",EDGE,"E132"),sQuery(id+"F0.wireOp",EDGE,"E133"),sQuery(id+"F0.wireOp",EDGE,"E134"),sQuery(id+"F0.wireOp",EDGE,"E135"),sQuery(id+"F0.wireOp",EDGE,"E136"),sQuery(id+"F0.wireOp",EDGE,"E137"),sQuery(id+"F0.wireOp",EDGE,"E138"),sQuery(id+"F0.wireOp",EDGE,"E139"),sQuery(id+"F0.wireOp",EDGE,"E140"),sQuery(id+"F0.wireOp",EDGE,"E142"),sQuery(id+"F0.wireOp",EDGE,"E143"),sQuery(id+"F0.wireOp",EDGE,"E144"),sQuery(id+"F0.wireOp",EDGE,"E145"),sQuery(id+"F0.wireOp",EDGE,"E146"),sQuery(id+"F0.wireOp",EDGE,"E147"),sQuery(id+"F0.wireOp",EDGE,"E148"),sQuery(id+"F0.wireOp",EDGE,"E149"),sQuery(id+"F0.wireOp",EDGE,"E150"),sQuery(id+"F0.wireOp",EDGE,"E151"),sQuery(id+"F0.wireOp",EDGE,"E152"),sQuery(id+"F0.wireOp",EDGE,"E153"),sQuery(id+"F0.wireOp",EDGE,"E154"),sQuery(id+"F0.wireOp",EDGE,"E155"),sQuery(id+"F0.wireOp",EDGE,"E156"),sQuery(id+"F0.wireOp",EDGE,"E157"),sQuery(id+"F0.wireOp",EDGE,"E158"),sQuery(id+"F0.wireOp",EDGE,"E159"),sQuery(id+"F0.wireOp",EDGE,"E160"),sQuery(id+"F0.wireOp",EDGE,"E161"),sQuery(id+"F0.wireOp",EDGE,"E162"),sQuery(id+"F0.wireOp",EDGE,"E163"),sQuery(id+"F0.wireOp",EDGE,"E164"),sQuery(id+"F0.wireOp",EDGE,"E165"),sQuery(id+"F0.wireOp",EDGE,"E166"),sQuery(id+"F0.wireOp",EDGE,"E167"),sQuery(id+"F0.wireOp",EDGE,"E168"),sQuery(id+"F0.wireOp",EDGE,"E169"),sQuery(id+"F0.wireOp",EDGE,"E170"),sQuery(id+"F0.wireOp",EDGE,"E171"),sQuery(id+"F0.wireOp",EDGE,"E172"),sQuery(id+"F0.wireOp",EDGE,"E173"),sQuery(id+"F0.wireOp",EDGE,"E174"),sQuery(id+"F0.wireOp",EDGE,"E179"),sQuery(id+"F0.wireOp",EDGE,"E180"),sQuery(id+"F0.wireOp",EDGE,"E181"),sQuery(id+"F0.wireOp",EDGE,"E182"),sQuery(id+"F0.wireOp",EDGE,"E183"),sQuery(id+"F0.wireOp",EDGE,"E184"),sQuery(id+"F0.wireOp",EDGE,"E185"),sQuery(id+"F0.wireOp",EDGE,"E186"),sQuery(id+"F0.wireOp",EDGE,"E187"),sQuery(id+"F0.wireOp",EDGE,"E188"),sQuery(id+"F0.wireOp",EDGE,"E198"),sQuery(id+"F0.wireOp",EDGE,"E199"),sQuery(id+"F0.wireOp",EDGE,"E200"),sQuery(id+"F0.wireOp",EDGE,"E201")])],"isStart":false});
            var sketch = newSketch(context, id + "F3", { "sketchPlane" : qUnion([Q0])});
            skArc(sketch, "E215", {"start": v(9.45, 36.83) * mm, "mid": v(1.7, 44.74) * mm, "end": v(-5.68, 36.49) * mm});
            skArc(sketch, "E216.0", {"start": v(5.64, 37) * mm, "mid": v(1.79, 40.93) * mm, "end": v(-1.89, 36.83) * mm});
            skSolve(sketch);
        }
        {
            var Q0;
            Q0 = qSketchRegion(id + "F3", true);
            var Q1;
            {var subQ0=sQuery(id+"F3.wireOp",EDGE,"E215");Q1=makeQuery(id+"F3.imprint","IMPRINT",FACE,{"disambiguationData":[TD([[makeQuery(id+"F3.imprint","IMPRINT",EDGE,{"derivedFrom":subQ0}),1.0]])]});}
            extrude(context, id + "F4", {"entities" : qUnion([Q0, Q1]), "operationType" : NewBodyOperationType.ADD, "oppositeDirection" : true, "depth" : 8.9 * mm, "offsetDistance" : 25.4 * mm});
        }
        {
            var Q0;
            {var subQ0=sQuery(id+"F3.wireOp",EDGE,"E215");Q0=makeQuery(id+"F3.imprint","IMPRINT",FACE,{"disambiguationData":[TD([[makeQuery(id+"F3.imprint","IMPRINT",EDGE,{"derivedFrom":subQ0}),1.0]])]});}
            extrude(context, id + "F5", {"entities" : qUnion([Q0]), "operationType" : NewBodyOperationType.REMOVE, "oppositeDirection" : true, "depth" : 2.54 * mm, "offsetDistance" : 25.4 * mm});
        }
    });
